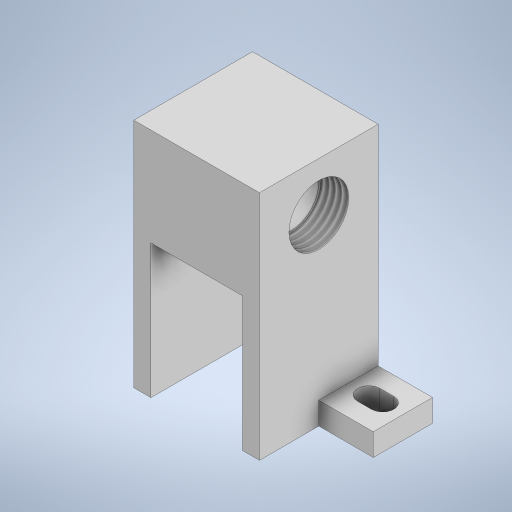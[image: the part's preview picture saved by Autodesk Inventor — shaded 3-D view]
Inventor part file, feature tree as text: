
AUTODESK INVENTOR PART (.ipt)
format: ipt  version: 2024.2 (Build 282272000, 272)  size: 304,640 bytes
history: native  units: in
note: dims shown in document units (in); Inventor stores cm internally (conversion verified against a paired STEP export)
features: sketch x7, extrude x5, hole x2
ambient origin geometry x8: Origin, YZ Plane, XZ Plane, XY Plane, X Axis, Y Axis, Z Axis, Center Point
bodies: Solid1 (feature_tree)
feature tree (14):
  extrude  "Extrusion1"  Depth=0.6693in
  extrude  "Extrusion2"  Depth=0.5157in
  extrude  "Extrusion3"  Depth=0.3071in
  extrude  "Extrusion4"  Depth=0.126in TaperAngle=0.0deg
  extrude  "Extrusion5"  Depth=0.126in
  hole  "Hole2"  [1 undecoded]
  hole  "Hole3"  [1 undecoded]
  sketch  "Sketch1"  dims[d0=0.7087in d1=0.6693in]
  sketch  "Sketch2"  dims[d2=1.3071in d3=0.0in d4=0.5157in]
  sketch  "Sketch4"  dims[d5=0.7559in d6=0.0in d7=0.3071in]
  sketch  "Sketch5"  dims[d8=0.3071in d9=0.126in d10=0.0in]
  sketch  "Sketch6"  dims[d11=0.1142in d12=0.126in]
  sketch  "Sketch8"  dims[d13=0.0787in d14=0.126in]
  sketch  "Sketch9"  dims[d15=0.0in d16=0.0in d17=0.1142in d18=0.0787in d19=0.126in d20=0.126in d21=0.2756in d22=0.315in d23=0.0in d24=0.0in d33=0.2756in d34=0.3372in d35=0.1575in d36=0.1575in d37=0.0787in d38=90.0deg d39=0.1575in d40=0.0in d41=0.2756in d42=0.3372in d43=0.1575in d44=0.1575in d45=0.0787in d46=90.0deg d47=0.1575in d48=0.0in]
note: 2 required parameter values undecoded (feature->parameter linkage not recoverable at this tier; creation-order binding heuristic only, values carry confidence <= 0.55)
